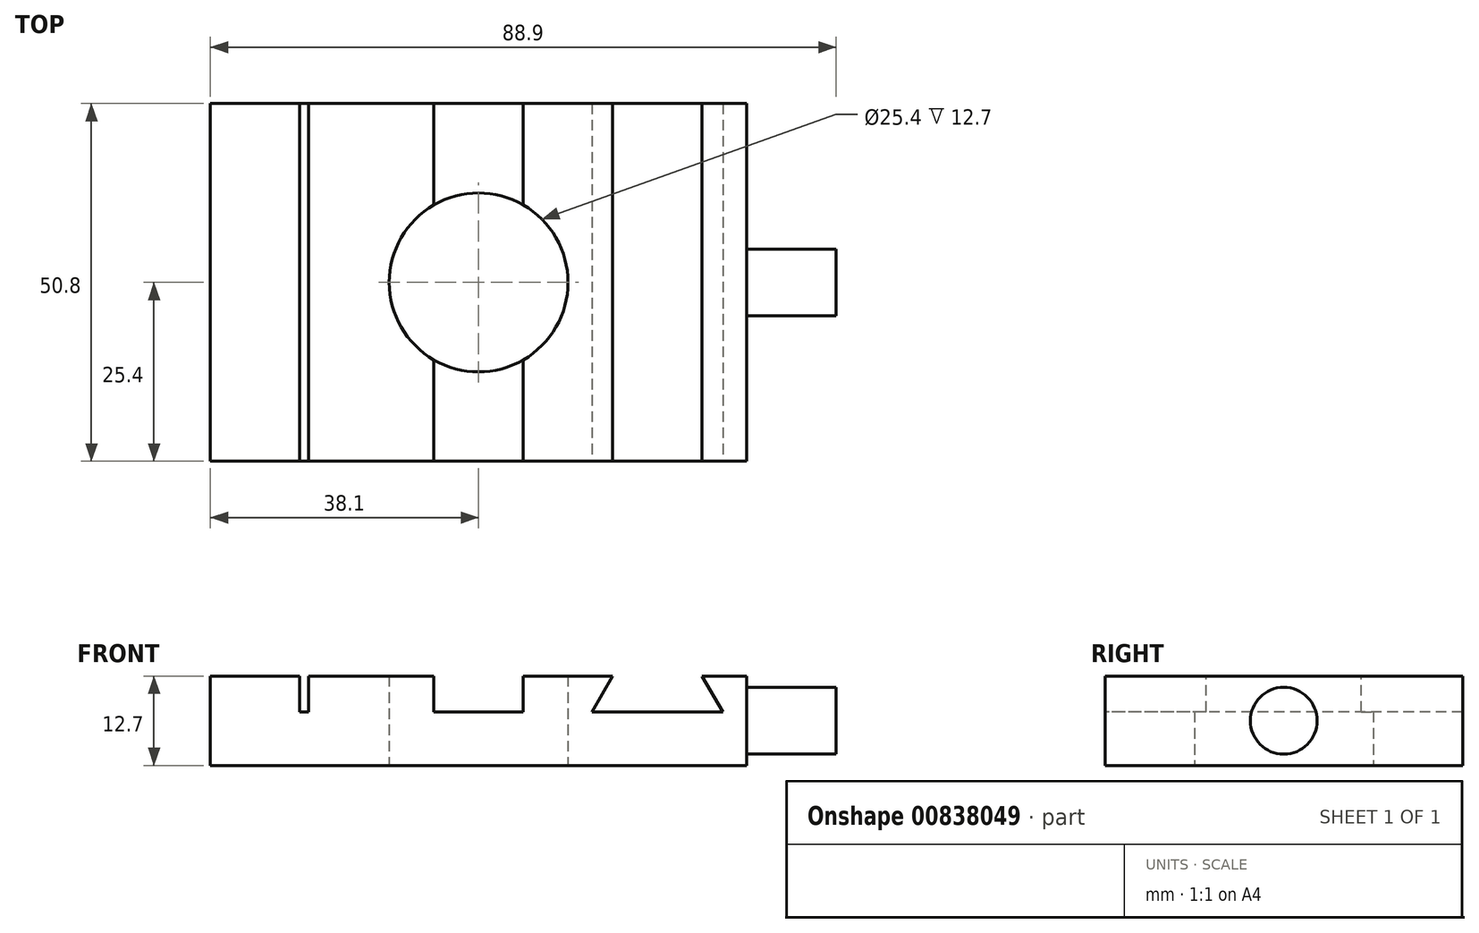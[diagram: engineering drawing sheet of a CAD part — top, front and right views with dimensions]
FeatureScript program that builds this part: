
annotation { "Feature Type Name" : "Feature", "Feature Type Description" : "" }
export const myFeature = defineFeature(function(context is Context, id is Id, definition is map)
    precondition{}
    {
        {
            var Q0;
            Q0=qCreatedBy(makeId("Top.planeOp"),FACE);
            var sketch = newSketch(context, id + "F0", { "sketchPlane" : qUnion([Q0])});
            skLineSegment(sketch, "E0.bottom", {"start": v(38.1, 25.4) * mm, "end": v(-38.1, 25.4) * mm});
            skLineSegment(sketch, "E0.top", {"start": v(38.1, -25.4) * mm, "end": v(-38.1, -25.4) * mm});
            skLineSegment(sketch, "E0.left", {"start": v(38.1, 25.4) * mm, "end": v(38.1, -25.4) * mm});
            skLineSegment(sketch, "E0.right", {"start": v(-38.1, 25.4) * mm, "end": v(-38.1, -25.4) * mm});
            skPoint(sketch, "E0.middle", {"position": v(0, 0) * mm});
            skCircle(sketch, "E1", {"center": v(0, 0) * mm, "radius": 12.7 * mm});
            skSolve(sketch);
        }
        {
            var Q0;
            Q0=makeQuery(id+"F0.imprint","IMPRINT",FACE,{"disambiguationData":[TD([[makeQuery(id+"F0.imprint","IMPRINT",EDGE,{"derivedFrom":sQuery(id+"F0.wireOp",EDGE,"E0.bottom")}),1.0]])]});
            extrude(context, id + "F1", {"entities" : qUnion([Q0]), "depth" : 12.7 * mm, "offsetDistance" : 25.4 * mm});
        }
        {
            var Q0;
            Q0=makeQuery(id+"F1.opExtrude","CAP_FACE",FACE,{"disambiguationData":[OSD([sQuery(id+"F0.wireOp",EDGE,"E0.bottom"),sQuery(id+"F0.wireOp",EDGE,"E0.top"),sQuery(id+"F0.wireOp",EDGE,"E0.left"),sQuery(id+"F0.wireOp",EDGE,"E0.right"),sQuery(id+"F0.wireOp",EDGE,"E1")])],"isStart":false});
            var sketch = newSketch(context, id + "F2", { "sketchPlane" : qUnion([Q0])});
            skLineSegment(sketch, "E2.bottom", {"start": v(-25.4, 25.4) * mm, "end": v(-24.13, 25.4) * mm});
            skLineSegment(sketch, "E2.top", {"start": v(-25.4, -25.4) * mm, "end": v(-24.13, -25.4) * mm});
            skLineSegment(sketch, "E2.left", {"start": v(-25.4, 25.4) * mm, "end": v(-25.4, -25.4) * mm});
            skLineSegment(sketch, "E2.right", {"start": v(-24.13, 25.4) * mm, "end": v(-24.13, -25.4) * mm});
            skLineSegment(sketch, "E3", {"start": v(-6.35, 25.4) * mm, "end": v(-6.35, -25.4) * mm});
            skLineSegment(sketch, "E4", {"start": v(6.35, 25.4) * mm, "end": v(6.35, -25.4) * mm});
            skPoint(sketch, "E5", {"position": v(0, 0) * mm});
            skLineSegment(sketch, "E6", {"start": v(-6.35, 25.4) * mm, "end": v(6.35, 25.4) * mm, "construction": true});
            skLineSegment(sketch, "E7", {"start": v(0, 25.4) * mm, "end": v(0, -25.4) * mm, "construction": true});
            skSolve(sketch);
        }
        {
            var Q0;
            {var subQ0=sQuery(id+"F2.wireOp",EDGE,"E3");var subQ1=makeQuery(id+"F1.opExtrude","CAP_EDGE",EDGE,{"disambiguationData":[OSD([sQuery(id+"F0.wireOp",EDGE,"E0.top")])],"isStart":false});var subQ2=makeQuery(id+"F2.imprint","INTERSECT",VERTEX,{"derivedFrom":[subQ1,subQ0]});Q0=makeQuery(id+"F2.imprint","IMPRINT",FACE,{"disambiguationData":[TD([[makeQuery(id+"F2.imprint","IMPRINT",EDGE,{"disambiguationData":[TD([[subQ2,1.0]])],"derivedFrom":subQ0}),1.0]])]});}
            var Q1;
            {var subQ0=sQuery(id+"F2.wireOp",EDGE,"E3");var subQ1=makeQuery(id+"F1.opExtrude","CAP_EDGE",EDGE,{"disambiguationData":[OSD([sQuery(id+"F0.wireOp",EDGE,"E0.bottom")])],"isStart":false});var subQ2=makeQuery(id+"F2.imprint","INTERSECT",VERTEX,{"derivedFrom":[subQ1,subQ0]});Q1=makeQuery(id+"F2.imprint","IMPRINT",FACE,{"disambiguationData":[TD([[makeQuery(id+"F2.imprint","IMPRINT",EDGE,{"disambiguationData":[TD([[subQ2,-1.0]])],"derivedFrom":subQ0}),1.0]])]});}
            var Q2;
            Q2=makeQuery(id+"F2.imprint","IMPRINT",FACE,{"disambiguationData":[TD([[makeQuery(id+"F2.imprint","IMPRINT",EDGE,{"derivedFrom":sQuery(id+"F2.wireOp",EDGE,"E2.bottom")}),1.0]])]});
            extrude(context, id + "F3", {"entities" : qUnion([Q0, Q1, Q2]), "operationType" : NewBodyOperationType.REMOVE, "oppositeDirection" : true, "depth" : 5.08 * mm, "offsetDistance" : 25.4 * mm});
        }
        {
            var Q0;
            Q0=makeQuery(id+"F1.opExtrude","SWEPT_FACE",FACE,{"disambiguationData":[OSD([sQuery(id+"F0.wireOp",EDGE,"E0.top")])]});
            var sketch = newSketch(context, id + "F4", { "sketchPlane" : qUnion([Q0])});
            skLineSegment(sketch, "E8", {"start": v(19.05, 12.7) * mm, "end": v(16.12, 7.62) * mm});
            skLineSegment(sketch, "E9", {"start": v(16.12, 7.62) * mm, "end": v(34.68, 7.62) * mm});
            skLineSegment(sketch, "E10", {"start": v(34.68, 7.62) * mm, "end": v(31.75, 12.7) * mm});
            skLineSegment(sketch, "E11", {"start": v(31.75, 12.7) * mm, "end": v(19.05, 12.7) * mm});
            skLineSegment(sketch, "E12", {"start": v(25.4, 7.62) * mm, "end": v(25.4, 12.7) * mm, "construction": true});
            skSolve(sketch);
        }
        {
            var Q0;
            Q0=makeQuery(id+"F4.imprint","IMPRINT",FACE,{"disambiguationData":[TD([[makeQuery(id+"F4.imprint","IMPRINT",EDGE,{"derivedFrom":sQuery(id+"F4.wireOp",EDGE,"E8")}),1.0]])]});
            extrude(context, id + "F5", {"entities" : qUnion([Q0]), "operationType" : NewBodyOperationType.REMOVE, "endBound" : BoundingType.THROUGH_ALL, "oppositeDirection" : true, "depth" : 25.4 * mm, "offsetDistance" : 25.4 * mm});
        }
        {
            var Q0;
            Q0=makeQuery(id+"F1.opExtrude","SWEPT_FACE",FACE,{"disambiguationData":[OSD([sQuery(id+"F0.wireOp",EDGE,"E0.left")])]});
            var sketch = newSketch(context, id + "F6", { "sketchPlane" : qUnion([Q0])});
            skCircle(sketch, "E13", {"center": v(0, 6.35) * mm, "radius": 4.75 * mm});
            skPoint(sketch, "E13.centerSnap0", {"position": v(-25.4, 6.35) * mm});
            skPoint(sketch, "E13.centerSnap1", {"position": v(0, 12.7) * mm});
            skSolve(sketch);
        }
        {
            var Q0;
            Q0=makeQuery(id+"F6.imprint","IMPRINT",FACE,{"disambiguationData":[TD([[makeQuery(id+"F6.imprint","IMPRINT",EDGE,{"derivedFrom":sQuery(id+"F6.wireOp",EDGE,"E13")}),1.0]])]});
            extrude(context, id + "F7", {"entities" : qUnion([Q0]), "operationType" : NewBodyOperationType.ADD, "depth" : 12.7 * mm, "offsetDistance" : 25.4 * mm});
        }
    });
